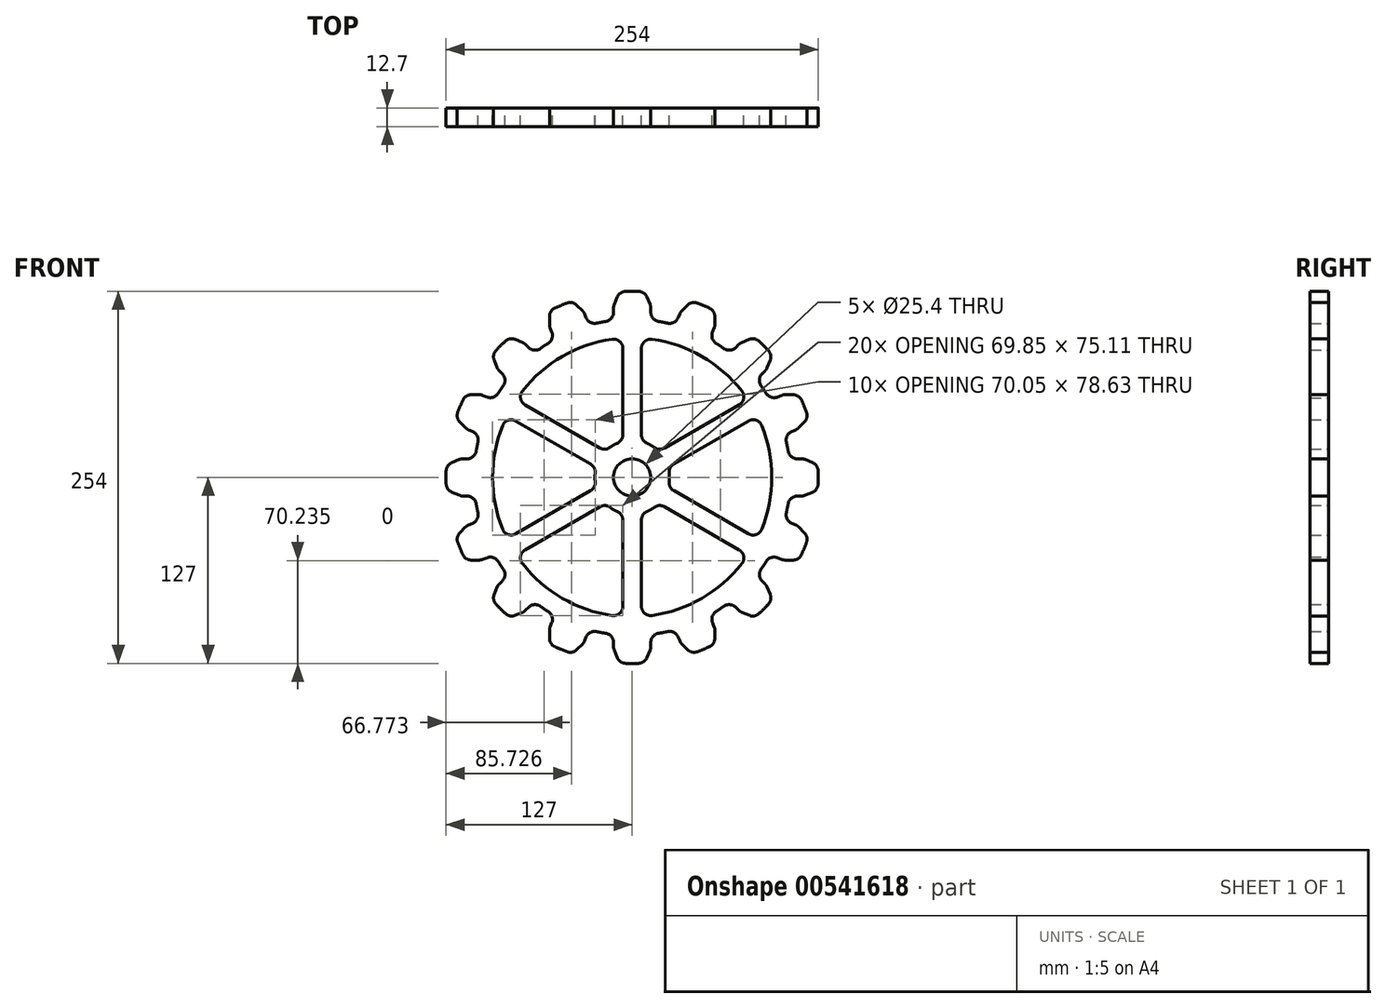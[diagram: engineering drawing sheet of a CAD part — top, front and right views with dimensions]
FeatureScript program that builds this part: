
annotation { "Feature Type Name" : "Feature", "Feature Type Description" : "" }
export const myFeature = defineFeature(function(context is Context, id is Id, definition is map)
    precondition{}
    {
        {
            var Q0;
            Q0=qCreatedBy(makeId("Front.planeOp"),FACE);
            var sketch = newSketch(context, id + "F0", { "sketchPlane" : qUnion([Q0])});
            skArc(sketch, "E0", {"start": v(-57.36, 91.45) * mm, "mid": v(-59.97, 89.76) * mm, "end": v(-62.54, 87.99) * mm});
            skCircle(sketch, "E1", {"center": v(0, 0) * mm, "radius": 12.7 * mm});
            skLineSegment(sketch, "E2", {"start": v(-12.7, 115.52) * mm, "end": v(-12.7, 112.7) * mm});
            skLineSegment(sketch, "E3", {"start": v(12.7, 115.52) * mm, "end": v(12.7, 112.7) * mm});
            skLineSegment(sketch, "E4", {"start": v(-12.22, 117.95) * mm, "end": v(-10.12, 123) * mm});
            skLineSegment(sketch, "E5", {"start": v(12.22, 117.95) * mm, "end": v(10.12, 123) * mm});
            skArc(sketch, "E6.trimOffspring", {"start": v(4.48, 126.92) * mm, "mid": v(0, 127) * mm, "end": v(-4.48, 126.92) * mm});
            skArc(sketch, "E7.filletArc", {"start": v(-4.48, 126.92) * mm, "mid": v(-7.88, 125.8) * mm, "end": v(-10.12, 123) * mm});
            skArc(sketch, "E8.filletArc", {"start": v(10.12, 123) * mm, "mid": v(7.88, 125.8) * mm, "end": v(4.48, 126.92) * mm});
            skPoint(sketch, "E9.visualSharp", {"position": v(-12.7, 116.78) * mm});
            skArc(sketch, "E9.filletArc", {"start": v(-12.22, 117.95) * mm, "mid": v(-12.58, 116.76) * mm, "end": v(-12.7, 115.52) * mm});
            skPoint(sketch, "E10.visualSharp", {"position": v(12.7, 116.78) * mm});
            skArc(sketch, "E10.filletArc", {"start": v(12.7, 115.52) * mm, "mid": v(12.58, 116.76) * mm, "end": v(12.22, 117.95) * mm});
            skLineSegment(sketch, "E11.1.0", {"start": v(55.94, 101.87) * mm, "end": v(54.86, 99.26) * mm});
            skArc(sketch, "E11.1.1", {"start": v(52.7, 115.55) * mm, "mid": v(48.6, 117.33) * mm, "end": v(44.43, 118.97) * mm});
            skArc(sketch, "E11.1.2", {"start": v(44.43, 118.97) * mm, "mid": v(40.86, 119.23) * mm, "end": v(37.72, 117.52) * mm});
            skArc(sketch, "E11.1.3", {"start": v(56.42, 109.77) * mm, "mid": v(55.41, 113.2) * mm, "end": v(52.7, 115.55) * mm});
            skPoint(sketch, "E11.1.4", {"position": v(32.96, 112.75) * mm});
            skPoint(sketch, "E11.1.5", {"position": v(56.42, 103.03) * mm});
            skLineSegment(sketch, "E11.1.6", {"start": v(32.47, 111.59) * mm, "end": v(31.4, 108.98) * mm});
            skLineSegment(sketch, "E11.1.7", {"start": v(33.85, 113.65) * mm, "end": v(37.72, 117.52) * mm});
            skLineSegment(sketch, "E11.1.8", {"start": v(56.42, 104.3) * mm, "end": v(56.42, 109.77) * mm});
            skArc(sketch, "E11.1.9", {"start": v(55.94, 101.87) * mm, "mid": v(56.3, 103.06) * mm, "end": v(56.42, 104.3) * mm});
            skArc(sketch, "E11.1.10", {"start": v(33.85, 113.65) * mm, "mid": v(33.06, 112.68) * mm, "end": v(32.47, 111.59) * mm});
            skLineSegment(sketch, "E11.2.0", {"start": v(90.66, 72.7) * mm, "end": v(88.67, 70.71) * mm});
            skArc(sketch, "E11.2.1", {"start": v(92.91, 86.58) * mm, "mid": v(89.8, 89.8) * mm, "end": v(86.58, 92.91) * mm});
            skArc(sketch, "E11.2.2", {"start": v(86.58, 92.91) * mm, "mid": v(83.38, 94.52) * mm, "end": v(79.82, 94.14) * mm});
            skArc(sketch, "E11.2.3", {"start": v(94.14, 79.82) * mm, "mid": v(94.52, 83.38) * mm, "end": v(92.91, 86.58) * mm});
            skPoint(sketch, "E11.2.4", {"position": v(73.6, 91.56) * mm});
            skPoint(sketch, "E11.2.5", {"position": v(91.56, 73.6) * mm});
            skLineSegment(sketch, "E11.2.6", {"start": v(72.7, 90.66) * mm, "end": v(70.71, 88.67) * mm});
            skLineSegment(sketch, "E11.2.7", {"start": v(74.76, 92.04) * mm, "end": v(79.82, 94.14) * mm});
            skLineSegment(sketch, "E11.2.8", {"start": v(92.04, 74.76) * mm, "end": v(94.14, 79.82) * mm});
            skArc(sketch, "E11.2.9", {"start": v(90.66, 72.7) * mm, "mid": v(91.45, 73.67) * mm, "end": v(92.04, 74.76) * mm});
            skArc(sketch, "E11.2.10", {"start": v(74.76, 92.04) * mm, "mid": v(73.67, 91.45) * mm, "end": v(72.7, 90.66) * mm});
            skLineSegment(sketch, "E11.3.0", {"start": v(111.59, 32.47) * mm, "end": v(108.98, 31.4) * mm});
            skArc(sketch, "E11.3.1", {"start": v(118.97, 44.43) * mm, "mid": v(117.33, 48.6) * mm, "end": v(115.55, 52.7) * mm});
            skArc(sketch, "E11.3.2", {"start": v(115.55, 52.7) * mm, "mid": v(113.2, 55.41) * mm, "end": v(109.77, 56.42) * mm});
            skArc(sketch, "E11.3.3", {"start": v(117.52, 37.72) * mm, "mid": v(119.23, 40.86) * mm, "end": v(118.97, 44.43) * mm});
            skPoint(sketch, "E11.3.4", {"position": v(103.03, 56.42) * mm});
            skPoint(sketch, "E11.3.5", {"position": v(112.75, 32.96) * mm});
            skLineSegment(sketch, "E11.3.6", {"start": v(101.87, 55.94) * mm, "end": v(99.26, 54.86) * mm});
            skLineSegment(sketch, "E11.3.7", {"start": v(104.3, 56.42) * mm, "end": v(109.77, 56.42) * mm});
            skLineSegment(sketch, "E11.3.8", {"start": v(113.65, 33.85) * mm, "end": v(117.52, 37.72) * mm});
            skArc(sketch, "E11.3.9", {"start": v(111.59, 32.47) * mm, "mid": v(112.68, 33.06) * mm, "end": v(113.65, 33.85) * mm});
            skArc(sketch, "E11.3.10", {"start": v(104.3, 56.42) * mm, "mid": v(103.06, 56.3) * mm, "end": v(101.87, 55.94) * mm});
            skLineSegment(sketch, "E11.4.0", {"start": v(115.52, -12.7) * mm, "end": v(112.7, -12.7) * mm});
            skArc(sketch, "E11.4.1", {"start": v(126.92, -4.48) * mm, "mid": v(127, 0) * mm, "end": v(126.92, 4.48) * mm});
            skArc(sketch, "E11.4.2", {"start": v(126.92, 4.48) * mm, "mid": v(125.8, 7.88) * mm, "end": v(123, 10.12) * mm});
            skArc(sketch, "E11.4.3", {"start": v(123, -10.12) * mm, "mid": v(125.8, -7.88) * mm, "end": v(126.92, -4.48) * mm});
            skPoint(sketch, "E11.4.4", {"position": v(116.78, 12.7) * mm});
            skPoint(sketch, "E11.4.5", {"position": v(116.78, -12.7) * mm});
            skLineSegment(sketch, "E11.4.6", {"start": v(115.52, 12.7) * mm, "end": v(112.7, 12.7) * mm});
            skLineSegment(sketch, "E11.4.7", {"start": v(117.95, 12.22) * mm, "end": v(123, 10.12) * mm});
            skLineSegment(sketch, "E11.4.8", {"start": v(117.95, -12.22) * mm, "end": v(123, -10.12) * mm});
            skArc(sketch, "E11.4.9", {"start": v(115.52, -12.7) * mm, "mid": v(116.76, -12.58) * mm, "end": v(117.95, -12.22) * mm});
            skArc(sketch, "E11.4.10", {"start": v(117.95, 12.22) * mm, "mid": v(116.76, 12.58) * mm, "end": v(115.52, 12.7) * mm});
            skLineSegment(sketch, "E11.5.0", {"start": v(101.87, -55.94) * mm, "end": v(99.26, -54.86) * mm});
            skArc(sketch, "E11.5.1", {"start": v(115.55, -52.7) * mm, "mid": v(117.33, -48.6) * mm, "end": v(118.97, -44.43) * mm});
            skArc(sketch, "E11.5.2", {"start": v(118.97, -44.43) * mm, "mid": v(119.23, -40.86) * mm, "end": v(117.52, -37.72) * mm});
            skArc(sketch, "E11.5.3", {"start": v(109.77, -56.42) * mm, "mid": v(113.2, -55.41) * mm, "end": v(115.55, -52.7) * mm});
            skPoint(sketch, "E11.5.4", {"position": v(112.75, -32.96) * mm});
            skPoint(sketch, "E11.5.5", {"position": v(103.03, -56.42) * mm});
            skLineSegment(sketch, "E11.5.6", {"start": v(111.59, -32.47) * mm, "end": v(108.98, -31.4) * mm});
            skLineSegment(sketch, "E11.5.7", {"start": v(113.65, -33.85) * mm, "end": v(117.52, -37.72) * mm});
            skLineSegment(sketch, "E11.5.8", {"start": v(104.3, -56.42) * mm, "end": v(109.77, -56.42) * mm});
            skArc(sketch, "E11.5.9", {"start": v(101.87, -55.94) * mm, "mid": v(103.06, -56.3) * mm, "end": v(104.3, -56.42) * mm});
            skArc(sketch, "E11.5.10", {"start": v(113.65, -33.85) * mm, "mid": v(112.68, -33.06) * mm, "end": v(111.59, -32.47) * mm});
            skLineSegment(sketch, "E11.6.0", {"start": v(72.7, -90.66) * mm, "end": v(70.71, -88.67) * mm});
            skArc(sketch, "E11.6.1", {"start": v(86.58, -92.91) * mm, "mid": v(89.8, -89.8) * mm, "end": v(92.91, -86.58) * mm});
            skArc(sketch, "E11.6.2", {"start": v(92.91, -86.58) * mm, "mid": v(94.52, -83.38) * mm, "end": v(94.14, -79.82) * mm});
            skArc(sketch, "E11.6.3", {"start": v(79.82, -94.14) * mm, "mid": v(83.38, -94.52) * mm, "end": v(86.58, -92.91) * mm});
            skPoint(sketch, "E11.6.4", {"position": v(91.56, -73.6) * mm});
            skPoint(sketch, "E11.6.5", {"position": v(73.6, -91.56) * mm});
            skLineSegment(sketch, "E11.6.6", {"start": v(90.66, -72.7) * mm, "end": v(88.67, -70.71) * mm});
            skLineSegment(sketch, "E11.6.7", {"start": v(92.04, -74.76) * mm, "end": v(94.14, -79.82) * mm});
            skLineSegment(sketch, "E11.6.8", {"start": v(74.76, -92.04) * mm, "end": v(79.82, -94.14) * mm});
            skArc(sketch, "E11.6.9", {"start": v(72.7, -90.66) * mm, "mid": v(73.67, -91.45) * mm, "end": v(74.76, -92.04) * mm});
            skArc(sketch, "E11.6.10", {"start": v(92.04, -74.76) * mm, "mid": v(91.45, -73.67) * mm, "end": v(90.66, -72.7) * mm});
            skLineSegment(sketch, "E11.7.0", {"start": v(32.47, -111.59) * mm, "end": v(31.4, -108.98) * mm});
            skArc(sketch, "E11.7.1", {"start": v(44.43, -118.97) * mm, "mid": v(48.6, -117.33) * mm, "end": v(52.7, -115.55) * mm});
            skArc(sketch, "E11.7.2", {"start": v(52.7, -115.55) * mm, "mid": v(55.41, -113.2) * mm, "end": v(56.42, -109.77) * mm});
            skArc(sketch, "E11.7.3", {"start": v(37.72, -117.52) * mm, "mid": v(40.86, -119.23) * mm, "end": v(44.43, -118.97) * mm});
            skPoint(sketch, "E11.7.4", {"position": v(56.42, -103.03) * mm});
            skPoint(sketch, "E11.7.5", {"position": v(32.96, -112.75) * mm});
            skLineSegment(sketch, "E11.7.6", {"start": v(55.94, -101.87) * mm, "end": v(54.86, -99.26) * mm});
            skLineSegment(sketch, "E11.7.7", {"start": v(56.42, -104.3) * mm, "end": v(56.42, -109.77) * mm});
            skLineSegment(sketch, "E11.7.8", {"start": v(33.85, -113.65) * mm, "end": v(37.72, -117.52) * mm});
            skArc(sketch, "E11.7.9", {"start": v(32.47, -111.59) * mm, "mid": v(33.06, -112.68) * mm, "end": v(33.85, -113.65) * mm});
            skArc(sketch, "E11.7.10", {"start": v(56.42, -104.3) * mm, "mid": v(56.3, -103.06) * mm, "end": v(55.94, -101.87) * mm});
            skLineSegment(sketch, "E11.8.0", {"start": v(-12.7, -115.52) * mm, "end": v(-12.7, -112.7) * mm});
            skArc(sketch, "E11.8.1", {"start": v(-4.48, -126.92) * mm, "mid": v(0, -127) * mm, "end": v(4.48, -126.92) * mm});
            skArc(sketch, "E11.8.2", {"start": v(4.48, -126.92) * mm, "mid": v(7.88, -125.8) * mm, "end": v(10.12, -123) * mm});
            skArc(sketch, "E11.8.3", {"start": v(-10.12, -123) * mm, "mid": v(-7.88, -125.8) * mm, "end": v(-4.48, -126.92) * mm});
            skPoint(sketch, "E11.8.4", {"position": v(12.7, -116.78) * mm});
            skPoint(sketch, "E11.8.5", {"position": v(-12.7, -116.78) * mm});
            skLineSegment(sketch, "E11.8.6", {"start": v(12.7, -115.52) * mm, "end": v(12.7, -112.7) * mm});
            skLineSegment(sketch, "E11.8.7", {"start": v(12.22, -117.95) * mm, "end": v(10.12, -123) * mm});
            skLineSegment(sketch, "E11.8.8", {"start": v(-12.22, -117.95) * mm, "end": v(-10.12, -123) * mm});
            skArc(sketch, "E11.8.9", {"start": v(-12.7, -115.52) * mm, "mid": v(-12.58, -116.76) * mm, "end": v(-12.22, -117.95) * mm});
            skArc(sketch, "E11.8.10", {"start": v(12.22, -117.95) * mm, "mid": v(12.58, -116.76) * mm, "end": v(12.7, -115.52) * mm});
            skLineSegment(sketch, "E11.9.0", {"start": v(-55.94, -101.87) * mm, "end": v(-54.86, -99.26) * mm});
            skArc(sketch, "E11.9.1", {"start": v(-52.7, -115.55) * mm, "mid": v(-48.6, -117.33) * mm, "end": v(-44.43, -118.97) * mm});
            skArc(sketch, "E11.9.2", {"start": v(-44.43, -118.97) * mm, "mid": v(-40.86, -119.23) * mm, "end": v(-37.72, -117.52) * mm});
            skArc(sketch, "E11.9.3", {"start": v(-56.42, -109.77) * mm, "mid": v(-55.41, -113.2) * mm, "end": v(-52.7, -115.55) * mm});
            skPoint(sketch, "E11.9.4", {"position": v(-32.96, -112.75) * mm});
            skPoint(sketch, "E11.9.5", {"position": v(-56.42, -103.03) * mm});
            skLineSegment(sketch, "E11.9.6", {"start": v(-32.47, -111.59) * mm, "end": v(-31.4, -108.98) * mm});
            skLineSegment(sketch, "E11.9.7", {"start": v(-33.85, -113.65) * mm, "end": v(-37.72, -117.52) * mm});
            skLineSegment(sketch, "E11.9.8", {"start": v(-56.42, -104.3) * mm, "end": v(-56.42, -109.77) * mm});
            skArc(sketch, "E11.9.9", {"start": v(-55.94, -101.87) * mm, "mid": v(-56.3, -103.06) * mm, "end": v(-56.42, -104.3) * mm});
            skArc(sketch, "E11.9.10", {"start": v(-33.85, -113.65) * mm, "mid": v(-33.06, -112.68) * mm, "end": v(-32.47, -111.59) * mm});
            skLineSegment(sketch, "E11.10.0", {"start": v(-90.66, -72.7) * mm, "end": v(-88.67, -70.71) * mm});
            skArc(sketch, "E11.10.1", {"start": v(-92.91, -86.58) * mm, "mid": v(-89.8, -89.8) * mm, "end": v(-86.58, -92.91) * mm});
            skArc(sketch, "E11.10.2", {"start": v(-86.58, -92.91) * mm, "mid": v(-83.38, -94.52) * mm, "end": v(-79.82, -94.14) * mm});
            skArc(sketch, "E11.10.3", {"start": v(-94.14, -79.82) * mm, "mid": v(-94.52, -83.38) * mm, "end": v(-92.91, -86.58) * mm});
            skPoint(sketch, "E11.10.4", {"position": v(-73.6, -91.56) * mm});
            skPoint(sketch, "E11.10.5", {"position": v(-91.56, -73.6) * mm});
            skLineSegment(sketch, "E11.10.6", {"start": v(-72.7, -90.66) * mm, "end": v(-70.71, -88.67) * mm});
            skLineSegment(sketch, "E11.10.7", {"start": v(-74.76, -92.04) * mm, "end": v(-79.82, -94.14) * mm});
            skLineSegment(sketch, "E11.10.8", {"start": v(-92.04, -74.76) * mm, "end": v(-94.14, -79.82) * mm});
            skArc(sketch, "E11.10.9", {"start": v(-90.66, -72.7) * mm, "mid": v(-91.45, -73.67) * mm, "end": v(-92.04, -74.76) * mm});
            skArc(sketch, "E11.10.10", {"start": v(-74.76, -92.04) * mm, "mid": v(-73.67, -91.45) * mm, "end": v(-72.7, -90.66) * mm});
            skLineSegment(sketch, "E11.11.0", {"start": v(-111.59, -32.47) * mm, "end": v(-108.98, -31.4) * mm});
            skArc(sketch, "E11.11.1", {"start": v(-118.97, -44.43) * mm, "mid": v(-117.33, -48.6) * mm, "end": v(-115.55, -52.7) * mm});
            skArc(sketch, "E11.11.2", {"start": v(-115.55, -52.7) * mm, "mid": v(-113.2, -55.41) * mm, "end": v(-109.77, -56.42) * mm});
            skArc(sketch, "E11.11.3", {"start": v(-117.52, -37.72) * mm, "mid": v(-119.23, -40.86) * mm, "end": v(-118.97, -44.43) * mm});
            skPoint(sketch, "E11.11.4", {"position": v(-103.03, -56.42) * mm});
            skPoint(sketch, "E11.11.5", {"position": v(-112.75, -32.96) * mm});
            skLineSegment(sketch, "E11.11.6", {"start": v(-101.87, -55.94) * mm, "end": v(-99.26, -54.86) * mm});
            skLineSegment(sketch, "E11.11.7", {"start": v(-104.3, -56.42) * mm, "end": v(-109.77, -56.42) * mm});
            skLineSegment(sketch, "E11.11.8", {"start": v(-113.65, -33.85) * mm, "end": v(-117.52, -37.72) * mm});
            skArc(sketch, "E11.11.9", {"start": v(-111.59, -32.47) * mm, "mid": v(-112.68, -33.06) * mm, "end": v(-113.65, -33.85) * mm});
            skArc(sketch, "E11.11.10", {"start": v(-104.3, -56.42) * mm, "mid": v(-103.06, -56.3) * mm, "end": v(-101.87, -55.94) * mm});
            skLineSegment(sketch, "E11.12.0", {"start": v(-115.52, 12.7) * mm, "end": v(-112.7, 12.7) * mm});
            skArc(sketch, "E11.12.1", {"start": v(-126.92, 4.48) * mm, "mid": v(-127, 0) * mm, "end": v(-126.92, -4.48) * mm});
            skArc(sketch, "E11.12.2", {"start": v(-126.92, -4.48) * mm, "mid": v(-125.8, -7.88) * mm, "end": v(-123, -10.12) * mm});
            skArc(sketch, "E11.12.3", {"start": v(-123, 10.12) * mm, "mid": v(-125.8, 7.88) * mm, "end": v(-126.92, 4.48) * mm});
            skPoint(sketch, "E11.12.4", {"position": v(-116.78, -12.7) * mm});
            skPoint(sketch, "E11.12.5", {"position": v(-116.78, 12.7) * mm});
            skLineSegment(sketch, "E11.12.6", {"start": v(-115.52, -12.7) * mm, "end": v(-112.7, -12.7) * mm});
            skLineSegment(sketch, "E11.12.7", {"start": v(-117.95, -12.22) * mm, "end": v(-123, -10.12) * mm});
            skLineSegment(sketch, "E11.12.8", {"start": v(-117.95, 12.22) * mm, "end": v(-123, 10.12) * mm});
            skArc(sketch, "E11.12.9", {"start": v(-115.52, 12.7) * mm, "mid": v(-116.76, 12.58) * mm, "end": v(-117.95, 12.22) * mm});
            skArc(sketch, "E11.12.10", {"start": v(-117.95, -12.22) * mm, "mid": v(-116.76, -12.58) * mm, "end": v(-115.52, -12.7) * mm});
            skLineSegment(sketch, "E11.13.0", {"start": v(-101.87, 55.94) * mm, "end": v(-99.26, 54.86) * mm});
            skArc(sketch, "E11.13.1", {"start": v(-115.55, 52.7) * mm, "mid": v(-117.33, 48.6) * mm, "end": v(-118.97, 44.43) * mm});
            skArc(sketch, "E11.13.2", {"start": v(-118.97, 44.43) * mm, "mid": v(-119.23, 40.86) * mm, "end": v(-117.52, 37.72) * mm});
            skArc(sketch, "E11.13.3", {"start": v(-109.77, 56.42) * mm, "mid": v(-113.2, 55.41) * mm, "end": v(-115.55, 52.7) * mm});
            skPoint(sketch, "E11.13.4", {"position": v(-112.75, 32.96) * mm});
            skPoint(sketch, "E11.13.5", {"position": v(-103.03, 56.42) * mm});
            skLineSegment(sketch, "E11.13.6", {"start": v(-111.59, 32.47) * mm, "end": v(-108.98, 31.4) * mm});
            skLineSegment(sketch, "E11.13.7", {"start": v(-113.65, 33.85) * mm, "end": v(-117.52, 37.72) * mm});
            skLineSegment(sketch, "E11.13.8", {"start": v(-104.3, 56.42) * mm, "end": v(-109.77, 56.42) * mm});
            skArc(sketch, "E11.13.9", {"start": v(-101.87, 55.94) * mm, "mid": v(-103.06, 56.3) * mm, "end": v(-104.3, 56.42) * mm});
            skArc(sketch, "E11.13.10", {"start": v(-113.65, 33.85) * mm, "mid": v(-112.68, 33.06) * mm, "end": v(-111.59, 32.47) * mm});
            skLineSegment(sketch, "E11.14.0", {"start": v(-72.7, 90.66) * mm, "end": v(-70.71, 88.67) * mm});
            skArc(sketch, "E11.14.1", {"start": v(-86.58, 92.91) * mm, "mid": v(-89.8, 89.8) * mm, "end": v(-92.91, 86.58) * mm});
            skArc(sketch, "E11.14.2", {"start": v(-92.91, 86.58) * mm, "mid": v(-94.52, 83.38) * mm, "end": v(-94.14, 79.82) * mm});
            skArc(sketch, "E11.14.3", {"start": v(-79.82, 94.14) * mm, "mid": v(-83.38, 94.52) * mm, "end": v(-86.58, 92.91) * mm});
            skPoint(sketch, "E11.14.4", {"position": v(-91.56, 73.6) * mm});
            skPoint(sketch, "E11.14.5", {"position": v(-73.6, 91.56) * mm});
            skLineSegment(sketch, "E11.14.6", {"start": v(-90.66, 72.7) * mm, "end": v(-88.67, 70.71) * mm});
            skLineSegment(sketch, "E11.14.7", {"start": v(-92.04, 74.76) * mm, "end": v(-94.14, 79.82) * mm});
            skLineSegment(sketch, "E11.14.8", {"start": v(-74.76, 92.04) * mm, "end": v(-79.82, 94.14) * mm});
            skArc(sketch, "E11.14.9", {"start": v(-72.7, 90.66) * mm, "mid": v(-73.67, 91.45) * mm, "end": v(-74.76, 92.04) * mm});
            skArc(sketch, "E11.14.10", {"start": v(-92.04, 74.76) * mm, "mid": v(-91.45, 73.67) * mm, "end": v(-90.66, 72.7) * mm});
            skLineSegment(sketch, "E11.15.0", {"start": v(-32.47, 111.59) * mm, "end": v(-31.4, 108.98) * mm});
            skArc(sketch, "E11.15.1", {"start": v(-44.43, 118.97) * mm, "mid": v(-48.6, 117.33) * mm, "end": v(-52.7, 115.55) * mm});
            skArc(sketch, "E11.15.2", {"start": v(-52.7, 115.55) * mm, "mid": v(-55.41, 113.2) * mm, "end": v(-56.42, 109.77) * mm});
            skArc(sketch, "E11.15.3", {"start": v(-37.72, 117.52) * mm, "mid": v(-40.86, 119.23) * mm, "end": v(-44.43, 118.97) * mm});
            skPoint(sketch, "E11.15.4", {"position": v(-56.42, 103.03) * mm});
            skPoint(sketch, "E11.15.5", {"position": v(-32.96, 112.75) * mm});
            skLineSegment(sketch, "E11.15.6", {"start": v(-55.94, 101.87) * mm, "end": v(-54.86, 99.26) * mm});
            skLineSegment(sketch, "E11.15.7", {"start": v(-56.42, 104.3) * mm, "end": v(-56.42, 109.77) * mm});
            skLineSegment(sketch, "E11.15.8", {"start": v(-33.85, 113.65) * mm, "end": v(-37.72, 117.52) * mm});
            skArc(sketch, "E11.15.9", {"start": v(-32.47, 111.59) * mm, "mid": v(-33.06, 112.68) * mm, "end": v(-33.85, 113.65) * mm});
            skArc(sketch, "E11.15.10", {"start": v(-56.42, 104.3) * mm, "mid": v(-56.3, 103.06) * mm, "end": v(-55.94, 101.87) * mm});
            skLineSegment(sketch, "E11.anchor1", {"start": v(0, 0) * mm, "end": v(-12.7, 107.2) * mm, "construction": true});
            skLineSegment(sketch, "E11.anchor2", {"start": v(0, 0) * mm, "end": v(-52.76, 94.18) * mm, "construction": true});
            skArc(sketch, "E12.trimOffspring", {"start": v(-18, 106.44) * mm, "mid": v(-21.06, 105.88) * mm, "end": v(-24.11, 105.22) * mm});
            skArc(sketch, "E13.trimOffspring", {"start": v(24.11, 105.22) * mm, "mid": v(21.06, 105.88) * mm, "end": v(18, 106.44) * mm});
            skArc(sketch, "E14.trimOffspring", {"start": v(62.54, 87.99) * mm, "mid": v(59.97, 89.76) * mm, "end": v(57.36, 91.45) * mm});
            skArc(sketch, "E15.trimOffspring", {"start": v(91.45, 57.36) * mm, "mid": v(89.76, 59.97) * mm, "end": v(87.99, 62.54) * mm});
            skArc(sketch, "E16.trimOffspring", {"start": v(106.44, 18) * mm, "mid": v(105.88, 21.06) * mm, "end": v(105.22, 24.11) * mm});
            skArc(sketch, "E17.trimOffspring", {"start": v(105.22, -24.11) * mm, "mid": v(105.88, -21.06) * mm, "end": v(106.44, -18) * mm});
            skArc(sketch, "E18.trimOffspring", {"start": v(87.99, -62.54) * mm, "mid": v(89.76, -59.97) * mm, "end": v(91.45, -57.36) * mm});
            skArc(sketch, "E19.trimOffspring", {"start": v(57.36, -91.45) * mm, "mid": v(59.97, -89.76) * mm, "end": v(62.54, -87.99) * mm});
            skArc(sketch, "E20.trimOffspring", {"start": v(18, -106.44) * mm, "mid": v(21.06, -105.88) * mm, "end": v(24.11, -105.22) * mm});
            skArc(sketch, "E21.trimOffspring", {"start": v(-24.11, -105.22) * mm, "mid": v(-21.06, -105.88) * mm, "end": v(-18, -106.44) * mm});
            skArc(sketch, "E22.trimOffspring", {"start": v(-62.54, -87.99) * mm, "mid": v(-59.97, -89.76) * mm, "end": v(-57.36, -91.45) * mm});
            skArc(sketch, "E23.trimOffspring", {"start": v(-91.45, -57.36) * mm, "mid": v(-89.76, -59.97) * mm, "end": v(-87.99, -62.54) * mm});
            skArc(sketch, "E24.trimOffspring", {"start": v(-106.44, -18) * mm, "mid": v(-105.88, -21.06) * mm, "end": v(-105.22, -24.11) * mm});
            skArc(sketch, "E25.trimOffspring", {"start": v(-105.22, 24.11) * mm, "mid": v(-105.88, 21.06) * mm, "end": v(-106.44, 18) * mm});
            skArc(sketch, "E26.trimOffspring", {"start": v(-87.99, 62.54) * mm, "mid": v(-89.76, 59.97) * mm, "end": v(-91.45, 57.36) * mm});
            skPoint(sketch, "E27.visualSharp", {"position": v(-66.82, 84.78) * mm});
            skArc(sketch, "E27.filletArc", {"start": v(-70.71, 88.67) * mm, "mid": v(-66.75, 86.83) * mm, "end": v(-62.54, 87.99) * mm});
            skPoint(sketch, "E28.visualSharp", {"position": v(-52.76, 94.18) * mm});
            skArc(sketch, "E28.filletArc", {"start": v(-57.36, 91.45) * mm, "mid": v(-54.68, 94.9) * mm, "end": v(-54.86, 99.26) * mm});
            skPoint(sketch, "E29.visualSharp", {"position": v(-29.3, 103.9) * mm});
            skArc(sketch, "E29.filletArc", {"start": v(-31.4, 108.98) * mm, "mid": v(-28.44, 105.77) * mm, "end": v(-24.11, 105.22) * mm});
            skPoint(sketch, "E30.visualSharp", {"position": v(-12.7, 107.2) * mm});
            skArc(sketch, "E30.filletArc", {"start": v(-18, 106.44) * mm, "mid": v(-14.2, 108.6) * mm, "end": v(-12.7, 112.7) * mm});
            skPoint(sketch, "E31.visualSharp", {"position": v(12.7, 107.2) * mm});
            skArc(sketch, "E31.filletArc", {"start": v(12.7, 112.7) * mm, "mid": v(14.2, 108.6) * mm, "end": v(18, 106.44) * mm});
            skPoint(sketch, "E32.visualSharp", {"position": v(29.3, 103.9) * mm});
            skArc(sketch, "E32.filletArc", {"start": v(24.11, 105.22) * mm, "mid": v(28.44, 105.77) * mm, "end": v(31.4, 108.98) * mm});
            skPoint(sketch, "E33.visualSharp", {"position": v(52.76, 94.18) * mm});
            skArc(sketch, "E33.filletArc", {"start": v(54.86, 99.26) * mm, "mid": v(54.68, 94.9) * mm, "end": v(57.36, 91.45) * mm});
            skPoint(sketch, "E34.visualSharp", {"position": v(66.82, 84.78) * mm});
            skArc(sketch, "E34.filletArc", {"start": v(62.54, 87.99) * mm, "mid": v(66.75, 86.83) * mm, "end": v(70.71, 88.67) * mm});
            skPoint(sketch, "E35.visualSharp", {"position": v(84.78, 66.82) * mm});
            skArc(sketch, "E35.filletArc", {"start": v(88.67, 70.71) * mm, "mid": v(86.83, 66.75) * mm, "end": v(87.99, 62.54) * mm});
            skPoint(sketch, "E36.visualSharp", {"position": v(94.18, 52.76) * mm});
            skArc(sketch, "E36.filletArc", {"start": v(91.45, 57.36) * mm, "mid": v(94.9, 54.68) * mm, "end": v(99.26, 54.86) * mm});
            skPoint(sketch, "E37.visualSharp", {"position": v(103.9, 29.3) * mm});
            skArc(sketch, "E37.filletArc", {"start": v(108.98, 31.4) * mm, "mid": v(105.77, 28.44) * mm, "end": v(105.22, 24.11) * mm});
            skPoint(sketch, "E38.visualSharp", {"position": v(107.2, 12.7) * mm});
            skArc(sketch, "E38.filletArc", {"start": v(106.44, 18) * mm, "mid": v(108.6, 14.2) * mm, "end": v(112.7, 12.7) * mm});
            skPoint(sketch, "E39.visualSharp", {"position": v(107.2, -12.7) * mm});
            skArc(sketch, "E39.filletArc", {"start": v(112.7, -12.7) * mm, "mid": v(108.6, -14.2) * mm, "end": v(106.44, -18) * mm});
            skPoint(sketch, "E40.visualSharp", {"position": v(103.9, -29.3) * mm});
            skArc(sketch, "E40.filletArc", {"start": v(105.22, -24.11) * mm, "mid": v(105.77, -28.44) * mm, "end": v(108.98, -31.4) * mm});
            skPoint(sketch, "E41.visualSharp", {"position": v(94.18, -52.76) * mm});
            skArc(sketch, "E41.filletArc", {"start": v(99.26, -54.86) * mm, "mid": v(94.9, -54.68) * mm, "end": v(91.45, -57.36) * mm});
            skPoint(sketch, "E42.visualSharp", {"position": v(84.78, -66.82) * mm});
            skArc(sketch, "E42.filletArc", {"start": v(87.99, -62.54) * mm, "mid": v(86.83, -66.75) * mm, "end": v(88.67, -70.71) * mm});
            skPoint(sketch, "E43.visualSharp", {"position": v(66.82, -84.78) * mm});
            skArc(sketch, "E43.filletArc", {"start": v(70.71, -88.67) * mm, "mid": v(66.75, -86.83) * mm, "end": v(62.54, -87.99) * mm});
            skPoint(sketch, "E44.visualSharp", {"position": v(52.76, -94.18) * mm});
            skArc(sketch, "E44.filletArc", {"start": v(57.36, -91.45) * mm, "mid": v(54.68, -94.9) * mm, "end": v(54.86, -99.26) * mm});
            skPoint(sketch, "E45.visualSharp", {"position": v(29.3, -103.9) * mm});
            skArc(sketch, "E45.filletArc", {"start": v(31.4, -108.98) * mm, "mid": v(28.44, -105.77) * mm, "end": v(24.11, -105.22) * mm});
            skPoint(sketch, "E46.visualSharp", {"position": v(12.7, -107.2) * mm});
            skArc(sketch, "E46.filletArc", {"start": v(18, -106.44) * mm, "mid": v(14.2, -108.6) * mm, "end": v(12.7, -112.7) * mm});
            skPoint(sketch, "E47.visualSharp", {"position": v(-12.7, -107.2) * mm});
            skArc(sketch, "E47.filletArc", {"start": v(-12.7, -112.7) * mm, "mid": v(-14.2, -108.6) * mm, "end": v(-18, -106.44) * mm});
            skPoint(sketch, "E48.visualSharp", {"position": v(-29.3, -103.9) * mm});
            skArc(sketch, "E48.filletArc", {"start": v(-24.11, -105.22) * mm, "mid": v(-28.44, -105.77) * mm, "end": v(-31.4, -108.98) * mm});
            skPoint(sketch, "E49.visualSharp", {"position": v(-52.76, -94.18) * mm});
            skArc(sketch, "E49.filletArc", {"start": v(-54.86, -99.26) * mm, "mid": v(-54.68, -94.9) * mm, "end": v(-57.36, -91.45) * mm});
            skPoint(sketch, "E50.visualSharp", {"position": v(-66.82, -84.78) * mm});
            skArc(sketch, "E50.filletArc", {"start": v(-62.54, -87.99) * mm, "mid": v(-66.75, -86.83) * mm, "end": v(-70.71, -88.67) * mm});
            skPoint(sketch, "E51.visualSharp", {"position": v(-84.78, -66.82) * mm});
            skArc(sketch, "E51.filletArc", {"start": v(-88.67, -70.71) * mm, "mid": v(-86.83, -66.75) * mm, "end": v(-87.99, -62.54) * mm});
            skPoint(sketch, "E52.visualSharp", {"position": v(-94.18, -52.76) * mm});
            skArc(sketch, "E52.filletArc", {"start": v(-91.45, -57.36) * mm, "mid": v(-94.9, -54.68) * mm, "end": v(-99.26, -54.86) * mm});
            skPoint(sketch, "E53.visualSharp", {"position": v(-103.9, -29.3) * mm});
            skArc(sketch, "E53.filletArc", {"start": v(-108.98, -31.4) * mm, "mid": v(-105.77, -28.44) * mm, "end": v(-105.22, -24.11) * mm});
            skPoint(sketch, "E54.visualSharp", {"position": v(-107.2, -12.7) * mm});
            skArc(sketch, "E54.filletArc", {"start": v(-106.44, -18) * mm, "mid": v(-108.6, -14.2) * mm, "end": v(-112.7, -12.7) * mm});
            skPoint(sketch, "E55.visualSharp", {"position": v(-107.2, 12.7) * mm});
            skArc(sketch, "E55.filletArc", {"start": v(-112.7, 12.7) * mm, "mid": v(-108.6, 14.2) * mm, "end": v(-106.44, 18) * mm});
            skPoint(sketch, "E56.visualSharp", {"position": v(-103.9, 29.3) * mm});
            skArc(sketch, "E56.filletArc", {"start": v(-105.22, 24.11) * mm, "mid": v(-105.77, 28.44) * mm, "end": v(-108.98, 31.4) * mm});
            skPoint(sketch, "E57.visualSharp", {"position": v(-94.18, 52.76) * mm});
            skArc(sketch, "E57.filletArc", {"start": v(-99.26, 54.86) * mm, "mid": v(-94.9, 54.68) * mm, "end": v(-91.45, 57.36) * mm});
            skPoint(sketch, "E58.visualSharp", {"position": v(-84.78, 66.82) * mm});
            skArc(sketch, "E58.filletArc", {"start": v(-87.99, 62.54) * mm, "mid": v(-86.83, 66.75) * mm, "end": v(-88.67, 70.71) * mm});
            skArc(sketch, "E59", {"start": v(-88.45, 35.35) * mm, "mid": v(-95.25, 0) * mm, "end": v(-88.45, -35.35) * mm});
            skLineSegment(sketch, "E60", {"start": v(79.38, -38.5) * mm, "end": v(28.38, -9.05) * mm});
            skLineSegment(sketch, "E61", {"start": v(73.03, -49.5) * mm, "end": v(22.03, -20.05) * mm});
            skLineSegment(sketch, "E62", {"start": v(-79.38, 38.5) * mm, "end": v(-28.38, 9.05) * mm});
            skLineSegment(sketch, "E63", {"start": v(-73.03, 49.5) * mm, "end": v(-22.03, 20.05) * mm});
            skLineSegment(sketch, "E64", {"start": v(-79.37, -38.5) * mm, "end": v(-28.38, -9.05) * mm});
            skLineSegment(sketch, "E65", {"start": v(-73.02, -49.5) * mm, "end": v(-22.03, -20.05) * mm});
            skArc(sketch, "E66", {"start": v(10.16, -23.28) * mm, "mid": v(12.7, -22) * mm, "end": v(15.08, -20.44) * mm});
            skPoint(sketch, "E67.orphan", {"position": v(-12.7, 0) * mm});
            skLineSegment(sketch, "E68.trimOffspring", {"start": v(22.03, 20.05) * mm, "end": v(73.02, 49.5) * mm});
            skLineSegment(sketch, "E69.trimOffspring", {"start": v(6.35, 29.1) * mm, "end": v(6.35, 87.99) * mm});
            skLineSegment(sketch, "E70.trimOffspring", {"start": v(-6.35, 29.1) * mm, "end": v(-6.35, 87.99) * mm});
            skLineSegment(sketch, "E71.trimOffspring", {"start": v(28.38, 9.05) * mm, "end": v(79.37, 38.5) * mm});
            skLineSegment(sketch, "E72.trimOffspring", {"start": v(-6.35, -29.1) * mm, "end": v(-6.35, -87.99) * mm});
            skLineSegment(sketch, "E73.trimOffspring", {"start": v(6.35, -29.1) * mm, "end": v(6.35, -87.99) * mm});
            skArc(sketch, "E74.trimOffspring", {"start": v(-74.84, -58.92) * mm, "mid": v(-47.62, -82.49) * mm, "end": v(-13.6, -94.27) * mm});
            skArc(sketch, "E75.trimOffspring", {"start": v(-13.6, 94.27) * mm, "mid": v(-47.63, 82.49) * mm, "end": v(-74.84, 58.92) * mm});
            skArc(sketch, "E76.trimOffspring", {"start": v(74.84, 58.92) * mm, "mid": v(47.62, 82.49) * mm, "end": v(13.6, 94.27) * mm});
            skArc(sketch, "E77.trimOffspring", {"start": v(88.45, -35.35) * mm, "mid": v(95.25, 0) * mm, "end": v(88.45, 35.35) * mm});
            skArc(sketch, "E78.trimOffspring", {"start": v(13.6, -94.27) * mm, "mid": v(47.63, -82.49) * mm, "end": v(74.84, -58.92) * mm});
            skArc(sketch, "E79.trimOffspring", {"start": v(25.24, -2.84) * mm, "mid": v(25.4, 0) * mm, "end": v(25.24, 2.84) * mm});
            skArc(sketch, "E80.trimOffspring", {"start": v(15.08, 20.44) * mm, "mid": v(12.7, 22) * mm, "end": v(10.16, 23.28) * mm});
            skArc(sketch, "E81.trimOffspring", {"start": v(-25.24, 2.84) * mm, "mid": v(-25.4, 0) * mm, "end": v(-25.24, -2.84) * mm});
            skArc(sketch, "E82.trimOffspring", {"start": v(-10.16, 23.28) * mm, "mid": v(-12.7, 22) * mm, "end": v(-15.08, 20.44) * mm});
            skArc(sketch, "E83.trimOffspring", {"start": v(-15.08, -20.44) * mm, "mid": v(-12.7, -22) * mm, "end": v(-10.16, -23.28) * mm});
            skPoint(sketch, "E84.visualSharp", {"position": v(-79.13, 53.02) * mm});
            skArc(sketch, "E84.filletArc", {"start": v(-74.84, 58.92) * mm, "mid": v(-76.09, 53.8) * mm, "end": v(-73.03, 49.5) * mm});
            skPoint(sketch, "E85.visualSharp", {"position": v(-85.48, 42.02) * mm});
            skArc(sketch, "E85.filletArc", {"start": v(-79.38, 38.5) * mm, "mid": v(-84.63, 39) * mm, "end": v(-88.45, 35.35) * mm});
            skPoint(sketch, "E86.visualSharp", {"position": v(-85.48, -42.02) * mm});
            skArc(sketch, "E86.filletArc", {"start": v(-88.45, -35.35) * mm, "mid": v(-84.63, -39) * mm, "end": v(-79.37, -38.5) * mm});
            skPoint(sketch, "E87.visualSharp", {"position": v(-79.13, -53.02) * mm});
            skArc(sketch, "E87.filletArc", {"start": v(-73.03, -49.5) * mm, "mid": v(-76.09, -53.8) * mm, "end": v(-74.84, -58.92) * mm});
            skPoint(sketch, "E88.visualSharp", {"position": v(-6.35, -95.04) * mm});
            skArc(sketch, "E88.filletArc", {"start": v(-13.6, -94.27) * mm, "mid": v(-8.54, -92.79) * mm, "end": v(-6.35, -87.99) * mm});
            skPoint(sketch, "E89.visualSharp", {"position": v(6.35, -95.04) * mm});
            skArc(sketch, "E89.filletArc", {"start": v(6.35, -87.99) * mm, "mid": v(8.54, -92.79) * mm, "end": v(13.6, -94.27) * mm});
            skPoint(sketch, "E90.visualSharp", {"position": v(79.13, -53.02) * mm});
            skArc(sketch, "E90.filletArc", {"start": v(74.84, -58.92) * mm, "mid": v(76.09, -53.8) * mm, "end": v(73.03, -49.5) * mm});
            skPoint(sketch, "E91.visualSharp", {"position": v(85.48, -42.02) * mm});
            skArc(sketch, "E91.filletArc", {"start": v(79.38, -38.5) * mm, "mid": v(84.63, -39) * mm, "end": v(88.45, -35.35) * mm});
            skPoint(sketch, "E92.visualSharp", {"position": v(85.48, 42.02) * mm});
            skArc(sketch, "E92.filletArc", {"start": v(88.45, 35.35) * mm, "mid": v(84.63, 39) * mm, "end": v(79.37, 38.5) * mm});
            skPoint(sketch, "E93.visualSharp", {"position": v(79.13, 53.02) * mm});
            skArc(sketch, "E93.filletArc", {"start": v(73.02, 49.5) * mm, "mid": v(76.09, 53.8) * mm, "end": v(74.84, 58.92) * mm});
            skPoint(sketch, "E94.visualSharp", {"position": v(6.35, 95.04) * mm});
            skArc(sketch, "E94.filletArc", {"start": v(13.6, 94.27) * mm, "mid": v(8.54, 92.79) * mm, "end": v(6.35, 87.99) * mm});
            skPoint(sketch, "E95.visualSharp", {"position": v(6.35, 24.6) * mm});
            skArc(sketch, "E95.filletArc", {"start": v(6.35, 29.1) * mm, "mid": v(7.39, 25.62) * mm, "end": v(10.16, 23.28) * mm});
            skPoint(sketch, "E96.visualSharp", {"position": v(-6.35, 95.04) * mm});
            skArc(sketch, "E96.filletArc", {"start": v(-6.35, 87.99) * mm, "mid": v(-8.54, 92.79) * mm, "end": v(-13.6, 94.27) * mm});
            skPoint(sketch, "E97.visualSharp", {"position": v(-18.12, 17.8) * mm});
            skArc(sketch, "E97.filletArc", {"start": v(-22.03, 20.05) * mm, "mid": v(-18.5, 19.2) * mm, "end": v(-15.08, 20.44) * mm});
            skPoint(sketch, "E98.visualSharp", {"position": v(-6.35, 24.6) * mm});
            skArc(sketch, "E98.filletArc", {"start": v(-10.16, 23.28) * mm, "mid": v(-7.39, 25.62) * mm, "end": v(-6.35, 29.1) * mm});
            skPoint(sketch, "E99.visualSharp", {"position": v(18.12, 17.8) * mm});
            skArc(sketch, "E99.filletArc", {"start": v(15.08, 20.44) * mm, "mid": v(18.5, 19.2) * mm, "end": v(22.03, 20.05) * mm});
            skPoint(sketch, "E100.visualSharp", {"position": v(24.47, 6.8) * mm});
            skArc(sketch, "E100.filletArc", {"start": v(28.38, 9.05) * mm, "mid": v(25.88, 6.41) * mm, "end": v(25.24, 2.84) * mm});
            skPoint(sketch, "E101.visualSharp", {"position": v(24.47, -6.8) * mm});
            skArc(sketch, "E101.filletArc", {"start": v(25.24, -2.84) * mm, "mid": v(25.88, -6.41) * mm, "end": v(28.38, -9.05) * mm});
            skPoint(sketch, "E102.visualSharp", {"position": v(18.12, -17.8) * mm});
            skArc(sketch, "E102.filletArc", {"start": v(22.03, -20.05) * mm, "mid": v(18.5, -19.2) * mm, "end": v(15.08, -20.44) * mm});
            skPoint(sketch, "E103.visualSharp", {"position": v(6.35, -24.6) * mm});
            skArc(sketch, "E103.filletArc", {"start": v(10.16, -23.28) * mm, "mid": v(7.39, -25.62) * mm, "end": v(6.35, -29.1) * mm});
            skPoint(sketch, "E104.visualSharp", {"position": v(-6.35, -24.6) * mm});
            skArc(sketch, "E104.filletArc", {"start": v(-6.35, -29.1) * mm, "mid": v(-7.39, -25.62) * mm, "end": v(-10.16, -23.28) * mm});
            skPoint(sketch, "E105.visualSharp", {"position": v(-18.12, -17.8) * mm});
            skArc(sketch, "E105.filletArc", {"start": v(-15.08, -20.44) * mm, "mid": v(-18.5, -19.2) * mm, "end": v(-22.03, -20.05) * mm});
            skPoint(sketch, "E106.visualSharp", {"position": v(-24.47, -6.8) * mm});
            skArc(sketch, "E106.filletArc", {"start": v(-28.38, -9.05) * mm, "mid": v(-25.88, -6.41) * mm, "end": v(-25.24, -2.84) * mm});
            skPoint(sketch, "E107.visualSharp", {"position": v(-24.47, 6.8) * mm});
            skArc(sketch, "E107.filletArc", {"start": v(-25.24, 2.84) * mm, "mid": v(-25.88, 6.41) * mm, "end": v(-28.38, 9.05) * mm});
            skSolve(sketch);
        }
        {
            var Q0;
            Q0 = qSketchRegion(id + "F0", true);
            extrude(context, id + "F1", {"entities" : qUnion([Q0]), "endBound" : BoundingType.SYMMETRIC, "depth" : 12.7 * mm, "offsetDistance" : 25.4 * mm});
        }
    });
